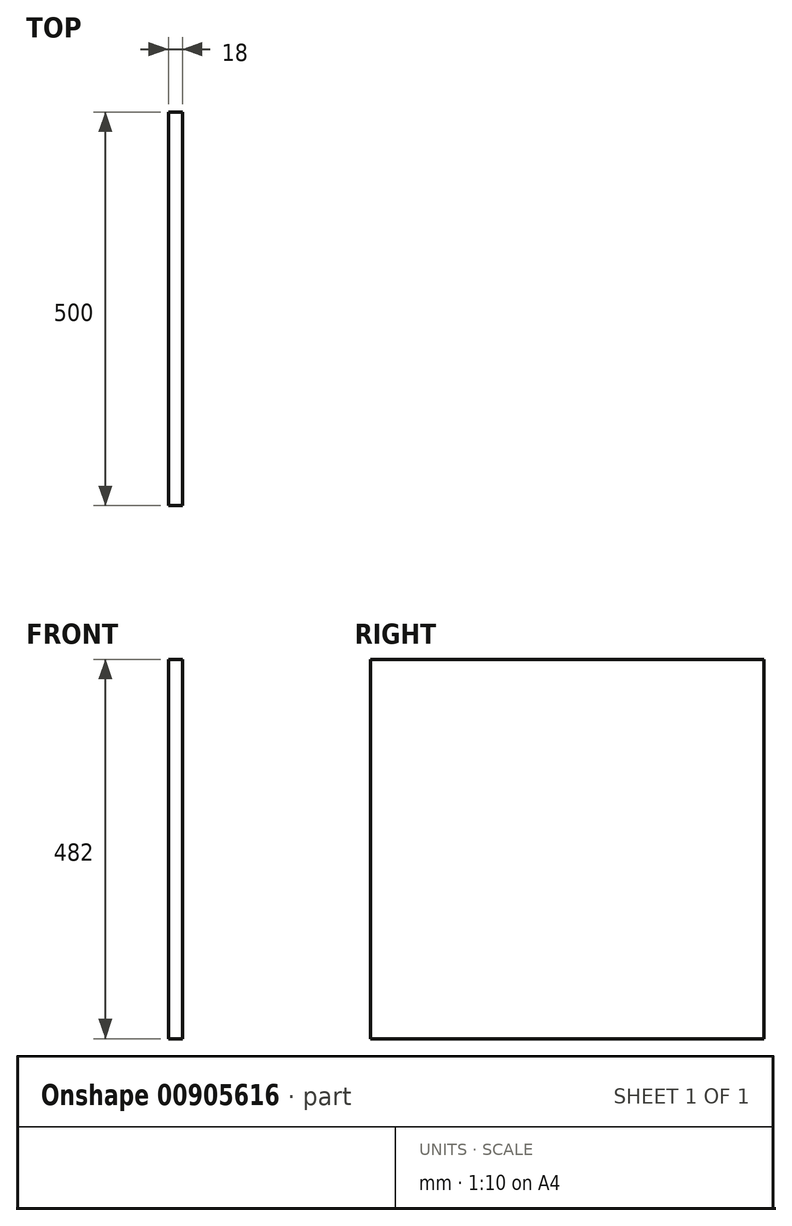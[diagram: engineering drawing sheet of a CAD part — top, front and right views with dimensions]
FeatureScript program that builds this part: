
annotation { "Feature Type Name" : "Feature", "Feature Type Description" : "" }
export const myFeature = defineFeature(function(context is Context, id is Id, definition is map)
    precondition{}
    {
        {
            var Q0;
            Q0=qCreatedBy(makeId("Right.planeOp"),FACE);
            var sketch = newSketch(context, id + "F0", { "sketchPlane" : qUnion([Q0])});
            skLineSegment(sketch, "E0.bottom", {"start": v(250, 241) * mm, "end": v(-250, 241) * mm});
            skLineSegment(sketch, "E0.top", {"start": v(250, -241) * mm, "end": v(-250, -241) * mm});
            skLineSegment(sketch, "E0.left", {"start": v(250, 241) * mm, "end": v(250, -241) * mm});
            skLineSegment(sketch, "E0.right", {"start": v(-250, 241) * mm, "end": v(-250, -241) * mm});
            skPoint(sketch, "E0.middle", {"position": v(0, 0) * mm});
            skSolve(sketch);
        }
        {
            var Q0;
            Q0=qSketchRegion(id+"F0",true);
            extrude(context, id + "F1", {"entities" : qUnion([Q0]), "depth" : 18 * mm, "offsetDistance" : 25 * mm});
        }
    });
